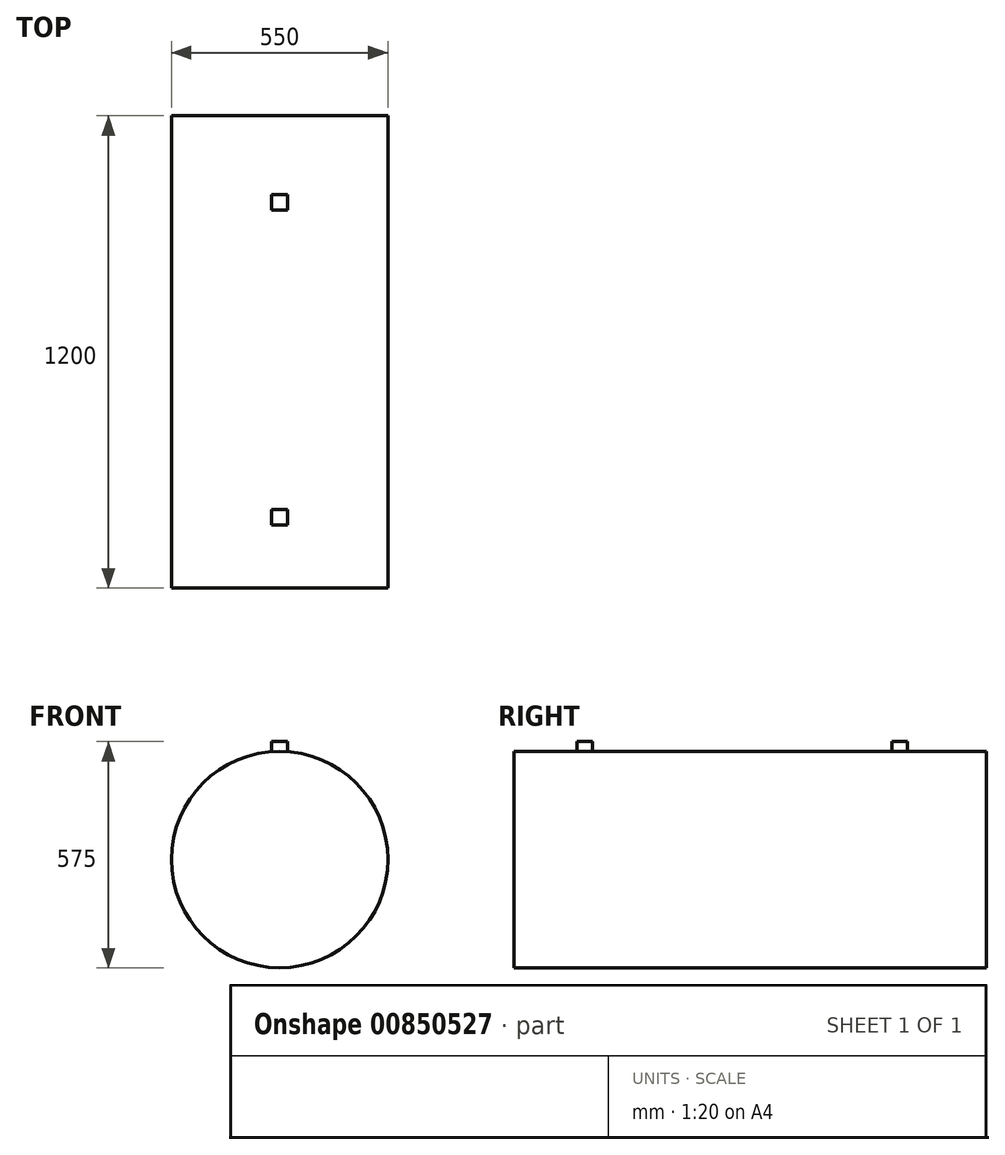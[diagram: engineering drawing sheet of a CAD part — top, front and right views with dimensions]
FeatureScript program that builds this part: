
annotation { "Feature Type Name" : "Feature", "Feature Type Description" : "" }
export const myFeature = defineFeature(function(context is Context, id is Id, definition is map)
    precondition{}
    {
        {
            var Q0;
            Q0=qCreatedBy(makeId("Front.planeOp"),FACE);
            var sketch = newSketch(context, id + "F0", { "sketchPlane" : qUnion([Q0])});
            skCircle(sketch, "E0", {"center": v(0, 0) * mm, "radius": 275 * mm});
            skSolve(sketch);
        }
        {
            var Q0;
            Q0=makeQuery(id+"F0.imprint","IMPRINT",FACE,{"disambiguationData":[TD([[makeQuery(id+"F0.imprint","IMPRINT",EDGE,{"derivedFrom":sQuery(id+"F0.wireOp",EDGE,"E0")}),1.0]])]});
            extrude(context, id + "F1", {"entities" : qUnion([Q0]), "depth" : 1200 * mm, "offsetDistance" : 25 * mm});
        }
        {
            var Q0;
            Q0=qCreatedBy(makeId("Top.planeOp"),FACE);
            var sketch = newSketch(context, id + "F2", { "sketchPlane" : qUnion([Q0])});
            skLineSegment(sketch, "E1.bottom", {"start": v(-20, -200) * mm, "end": v(20, -200) * mm});
            skLineSegment(sketch, "E1.top", {"start": v(-20, -240) * mm, "end": v(20, -240) * mm});
            skLineSegment(sketch, "E1.left", {"start": v(-20, -200) * mm, "end": v(-20, -240) * mm});
            skLineSegment(sketch, "E1.right", {"start": v(20, -200) * mm, "end": v(20, -240) * mm});
            skLineSegment(sketch, "E2.0.1.0", {"start": v(20, -1000) * mm, "end": v(20, -1040) * mm});
            skLineSegment(sketch, "E2.0.1.1", {"start": v(-20, -1000) * mm, "end": v(20, -1000) * mm});
            skLineSegment(sketch, "E2.0.1.2", {"start": v(-20, -1000) * mm, "end": v(-20, -1040) * mm});
            skLineSegment(sketch, "E2.0.1.3", {"start": v(-20, -1040) * mm, "end": v(20, -1040) * mm});
            skLineSegment(sketch, "E2.direction1", {"start": v(20, -240) * mm, "end": v(45, -240) * mm, "construction": true});
            skLineSegment(sketch, "E2.direction2", {"start": v(20, -240) * mm, "end": v(20, -1040) * mm, "construction": true});
            skSolve(sketch);
        }
        {
            var Q0;
            Q0 = qSketchRegion(id + "F2", true);
            extrude(context, id + "F3", {"entities" : qUnion([Q0]), "operationType" : NewBodyOperationType.ADD, "depth" : 300 * mm, "offsetDistance" : 25 * mm});
        }
    });
